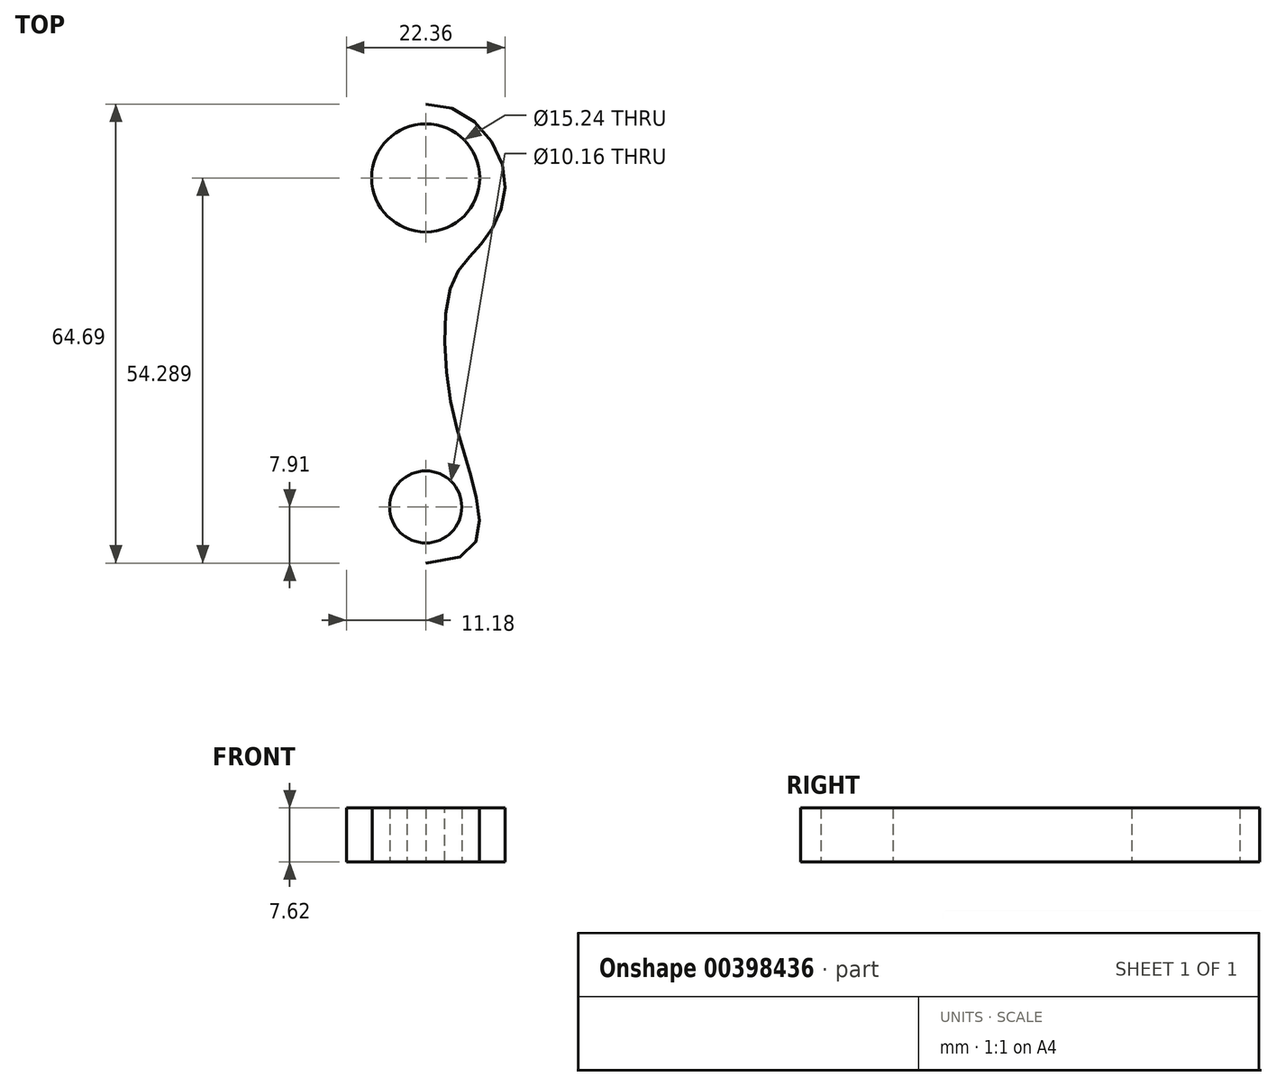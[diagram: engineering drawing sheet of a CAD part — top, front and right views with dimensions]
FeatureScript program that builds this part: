
annotation { "Feature Type Name" : "Feature", "Feature Type Description" : "" }
export const myFeature = defineFeature(function(context is Context, id is Id, definition is map)
    precondition{}
    {
        {
            var Q0;
            Q0=qCreatedBy(makeId("Top.planeOp"),FACE);
            var sketch = newSketch(context, id + "F0", { "sketchPlane" : qUnion([Q0])});
            skCircle(sketch, "E0", {"center": v(0, 46.38) * mm, "radius": 7.62 * mm});
            skCircle(sketch, "E1", {"center": v(0, 0) * mm, "radius": 5.08 * mm});
            skFitSpline(sketch, "E2", {"points": [v(0, 56.76) * mm, v(-10.86, 48.03) * mm, v(-8.5, 37.88) * mm, v(-3.76, 31.7) * mm, v(-3.76, 13.65) * mm, v(-7.38, 0) * mm, v(0, -7.9) * mm], "startDerivative": vector(-88.6, 5.9) * mm, "endDerivative": vector(147.02, 0) * mm});
            skFitSpline(sketch, "E3.MirrorCS", {"points": [v(0, 56.76) * mm, v(10.86, 48.03) * mm, v(8.5, 37.88) * mm, v(3.76, 31.7) * mm, v(3.76, 13.65) * mm, v(7.38, 0) * mm, v(0, -7.9) * mm], "startDerivative": vector(88.6, 5.9) * mm, "endDerivative": vector(-147.02, 0) * mm});
            skSolve(sketch);
        }
        {
            var Q0;
            Q0 = qSketchRegion(id + "F0", true);
            extrude(context, id + "F1", {"entities" : qUnion([Q0]), "depth" : 7.62 * mm});
        }
    });
